# Revit family: 207014 TERRA MEDIUM WALL-WASHER
name_source: partatom
category: Apparecchi per illuminazione
units: mm (PartAtom-declared; Revit-internal decimal feet)

## family parameters
Basato su piano di lavoro = No
Condiviso = Sì
Mantieni orientamento annotazione = No
Punto di calcolo locali = No
Quota connettore circolare = Usa diametro
Sempre verticale = Sì
Sorgente d'illuminazione = Sì
Taglio con vuoti quando caricato = No
Tipo di parte = Normale

## types (1)
- ALLOY
    Angolo inclinazione = 15.00°
    Available Optics = WALL-WASHER
    Colori = 3000°K    4000°K
    Commenti sul wattaggio = CLASS I
    Files diagrammi fotometrici = https://puk.it
    Filtro dei colori = 16777215
    Finish color = STAINLESS STEEL. AISI 316L
    IK Rating = IK10
    IP Rating = IP67
    Ligjt Source = LED
    Material = High corrosion resistance die-cast copper-free aluminum body
    Modello = TERRA MEDIUM WALL-WASHER
    Produttore = PUK
    Prospetto di default = 0 mm  [stored 0 ft]
    URL = https://puk.it
    Variazione temperatura colore lampada con luminosità attenuata = <Nessuno>
    Voltage = 220-240V 50-60Hz
    Wattage = 13W

note: [stored X ft] marks values corroborated as IEEE doubles in the binary element streams (Revit-internal decimal feet)
